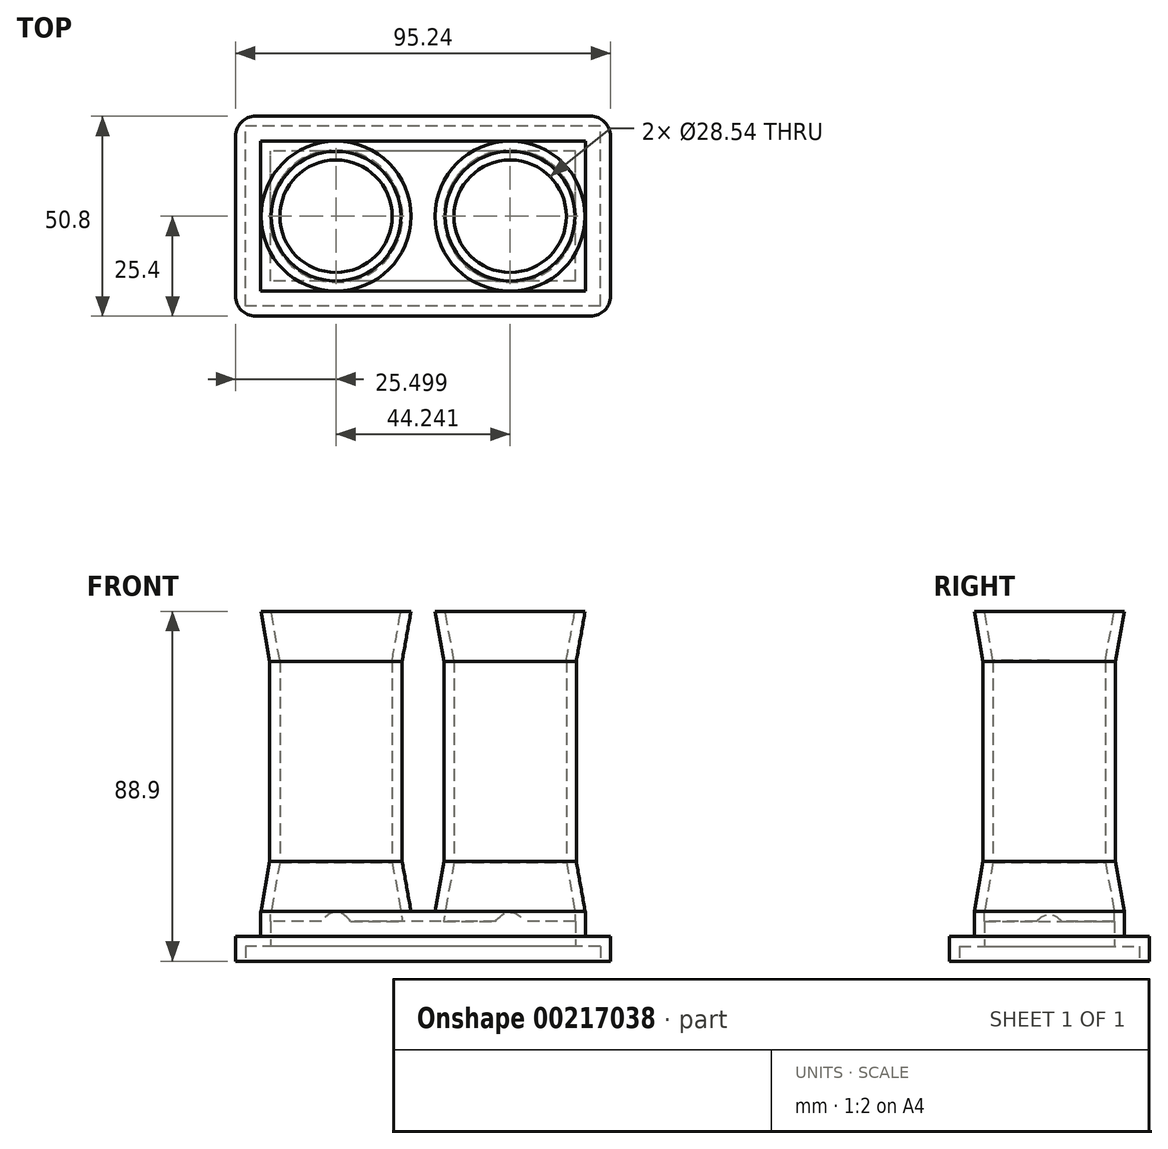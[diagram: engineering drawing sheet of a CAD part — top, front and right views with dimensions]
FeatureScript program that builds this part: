
annotation { "Feature Type Name" : "Feature", "Feature Type Description" : "" }
export const myFeature = defineFeature(function(context is Context, id is Id, definition is map)
    precondition{}
    {
        {
            var Q0;
            Q0=qCreatedBy(makeId("Top.planeOp"),FACE);
            var sketch = newSketch(context, id + "F0", { "sketchPlane" : qUnion([Q0])});
            skLineSegment(sketch, "E0.bottom", {"start": v(47.63, -25.4) * mm, "end": v(-47.63, -25.4) * mm});
            skLineSegment(sketch, "E0.top", {"start": v(47.63, 25.4) * mm, "end": v(-47.63, 25.4) * mm});
            skLineSegment(sketch, "E0.left", {"start": v(47.63, -25.4) * mm, "end": v(47.63, 25.4) * mm});
            skLineSegment(sketch, "E0.right", {"start": v(-47.63, -25.4) * mm, "end": v(-47.63, 25.4) * mm});
            skPoint(sketch, "E0.middle", {"position": v(0, 0) * mm});
            skSolve(sketch);
        }
        {
            var Q0;
            Q0 = qSketchRegion(id + "F0", true);
            extrude(context, id + "F1", {"entities" : qUnion([Q0]), "depth" : 6.35 * mm});
        }
        {
            var Q0;
            Q0=makeQuery(id+"F1.opExtrude","CAP_FACE",FACE,{"disambiguationData":[OSD([sQuery(id+"F0.wireOp",EDGE,"E0.bottom"),sQuery(id+"F0.wireOp",EDGE,"E0.top"),sQuery(id+"F0.wireOp",EDGE,"E0.left"),sQuery(id+"F0.wireOp",EDGE,"E0.right")])],"isStart":false});
            var sketch = newSketch(context, id + "F2", { "sketchPlane" : qUnion([Q0])});
            skLineSegment(sketch, "E1.bottom", {"start": v(41.28, -19.05) * mm, "end": v(-41.28, -19.05) * mm});
            skLineSegment(sketch, "E1.top", {"start": v(41.28, 19.05) * mm, "end": v(-41.28, 19.05) * mm});
            skLineSegment(sketch, "E1.left", {"start": v(41.28, -19.05) * mm, "end": v(41.28, 19.05) * mm});
            skLineSegment(sketch, "E1.right", {"start": v(-41.28, -19.05) * mm, "end": v(-41.28, 19.05) * mm});
            skPoint(sketch, "E1.middle", {"position": v(0, 0) * mm});
            skSolve(sketch);
        }
        {
            var Q0;
            Q0=makeQuery(id+"F2.imprint","IMPRINT",FACE,{"disambiguationData":[TD([[makeQuery(id+"F2.imprint","IMPRINT",EDGE,{"derivedFrom":sQuery(id+"F2.wireOp",EDGE,"E1.bottom")}),-1.0]])]});
            extrude(context, id + "F3", {"entities" : qUnion([Q0]), "operationType" : NewBodyOperationType.ADD, "depth" : 6.35 * mm});
        }
        {
            var Q0;
            Q0=makeQuery(id+"F3.opExtrude","CAP_FACE",FACE,{"disambiguationData":[OSD([sQuery(id+"F2.wireOp",EDGE,"E1.bottom"),sQuery(id+"F2.wireOp",EDGE,"E1.top"),sQuery(id+"F2.wireOp",EDGE,"E1.left"),sQuery(id+"F2.wireOp",EDGE,"E1.right")])],"isStart":false});
            var sketch = newSketch(context, id + "F4", { "sketchPlane" : qUnion([Q0])});
            skCircle(sketch, "E2", {"center": v(-22.12, 0) * mm, "radius": 19.05 * mm});
            skPoint(sketch, "E2.centerSnap0", {"position": v(-41.28, 0) * mm});
            skCircle(sketch, "E3.MirrorC", {"center": v(22.12, 0) * mm, "radius": 19.05 * mm});
            skLineSegment(sketch, "E4", {"start": v(-22.12, 0) * mm, "end": v(22.12, 0) * mm, "construction": true});
            skSolve(sketch);
        }
        {
            var Q0;
            Q0 = qSketchRegion(id + "F4", true);
            extrude(context, id + "F5", {"entities" : qUnion([Q0]), "operationType" : NewBodyOperationType.ADD, "depth" : 12.7 * mm, "hasDraft" : true, "draftAngle" : 10 * degree, "draftPullDirection" : true});
        }
        {
            var Q0;
            Q0=makeQuery(id+"F5.opExtrude","CAP_FACE",FACE,{"disambiguationData":[OSD([sQuery(id+"F4.wireOp",EDGE,"E2")])],"isStart":false});
            var Q1;
            Q1=makeQuery(id+"F5.opExtrude","CAP_FACE",FACE,{"disambiguationData":[OSD([sQuery(id+"F4.wireOp",EDGE,"E3.MirrorC")])],"isStart":false});
            extrude(context, id + "F6", {"entities" : qUnion([Q0, Q1]), "operationType" : NewBodyOperationType.ADD, "depth" : 50.8 * mm});
        }
        {
            var Q0;
            Q0=makeQuery(id+"F6.opExtrude","CAP_FACE",FACE,{"disambiguationData":[OSD([sQuery(id+"F4.wireOp",EDGE,"E3.MirrorC")])],"isStart":false});
            var Q1;
            Q1=makeQuery(id+"F6.opExtrude","CAP_FACE",FACE,{"disambiguationData":[OSD([sQuery(id+"F4.wireOp",EDGE,"E2")])],"isStart":false});
            extrude(context, id + "F7", {"entities" : qUnion([Q0, Q1]), "operationType" : NewBodyOperationType.ADD, "depth" : 12.7 * mm, "hasDraft" : true, "draftAngle" : 10 * degree});
        }
        {
            var Q0;
            Q0=makeQuery(id+"F7.opExtrude","CAP_FACE",FACE,{"disambiguationData":[OSD([sQuery(id+"F4.wireOp",EDGE,"E2")])],"isStart":false});
            var Q1;
            Q1=makeQuery(id+"F7.opExtrude","CAP_FACE",FACE,{"disambiguationData":[OSD([sQuery(id+"F4.wireOp",EDGE,"E3.MirrorC")])],"isStart":false});
            var Q2;
            Q2=makeQuery(id+"F1.opExtrude","CAP_FACE",FACE,{"disambiguationData":[OSD([sQuery(id+"F0.wireOp",EDGE,"E0.bottom"),sQuery(id+"F0.wireOp",EDGE,"E0.top"),sQuery(id+"F0.wireOp",EDGE,"E0.left"),sQuery(id+"F0.wireOp",EDGE,"E0.right")])],"isStart":true});
            shell(context, id + "F8", {"entities" : qUnion([Q0, Q1, Q2]), "thickness" : 2.54 * mm});
        }
        {
            var Q0;
            Q0=makeQuery(id+"F1.opExtrude","SWEPT_EDGE",EDGE,{"disambiguationData":[OSD([sQuery(id+"F0.wireOp",EDGE,"E0.bottom"),sQuery(id+"F0.wireOp",EDGE,"E0.right")])]});
            var Q1;
            Q1=makeQuery(id+"F1.opExtrude","SWEPT_EDGE",EDGE,{"disambiguationData":[OSD([sQuery(id+"F0.wireOp",EDGE,"E0.bottom"),sQuery(id+"F0.wireOp",EDGE,"E0.left")])]});
            var Q2;
            Q2=makeQuery(id+"F1.opExtrude","SWEPT_EDGE",EDGE,{"disambiguationData":[OSD([sQuery(id+"F0.wireOp",EDGE,"E0.top"),sQuery(id+"F0.wireOp",EDGE,"E0.left")])]});
            var Q3;
            Q3=makeQuery(id+"F1.opExtrude","SWEPT_EDGE",EDGE,{"disambiguationData":[OSD([sQuery(id+"F0.wireOp",EDGE,"E0.top"),sQuery(id+"F0.wireOp",EDGE,"E0.right")])]});
            fillet(context, id + "F9", {"entities" : qUnion([Q0, Q1, Q2, Q3]), "radius" : 5.08 * mm, "tangentPropagation" : true, "allowEdgeOverflow" : false});
        }
    });
